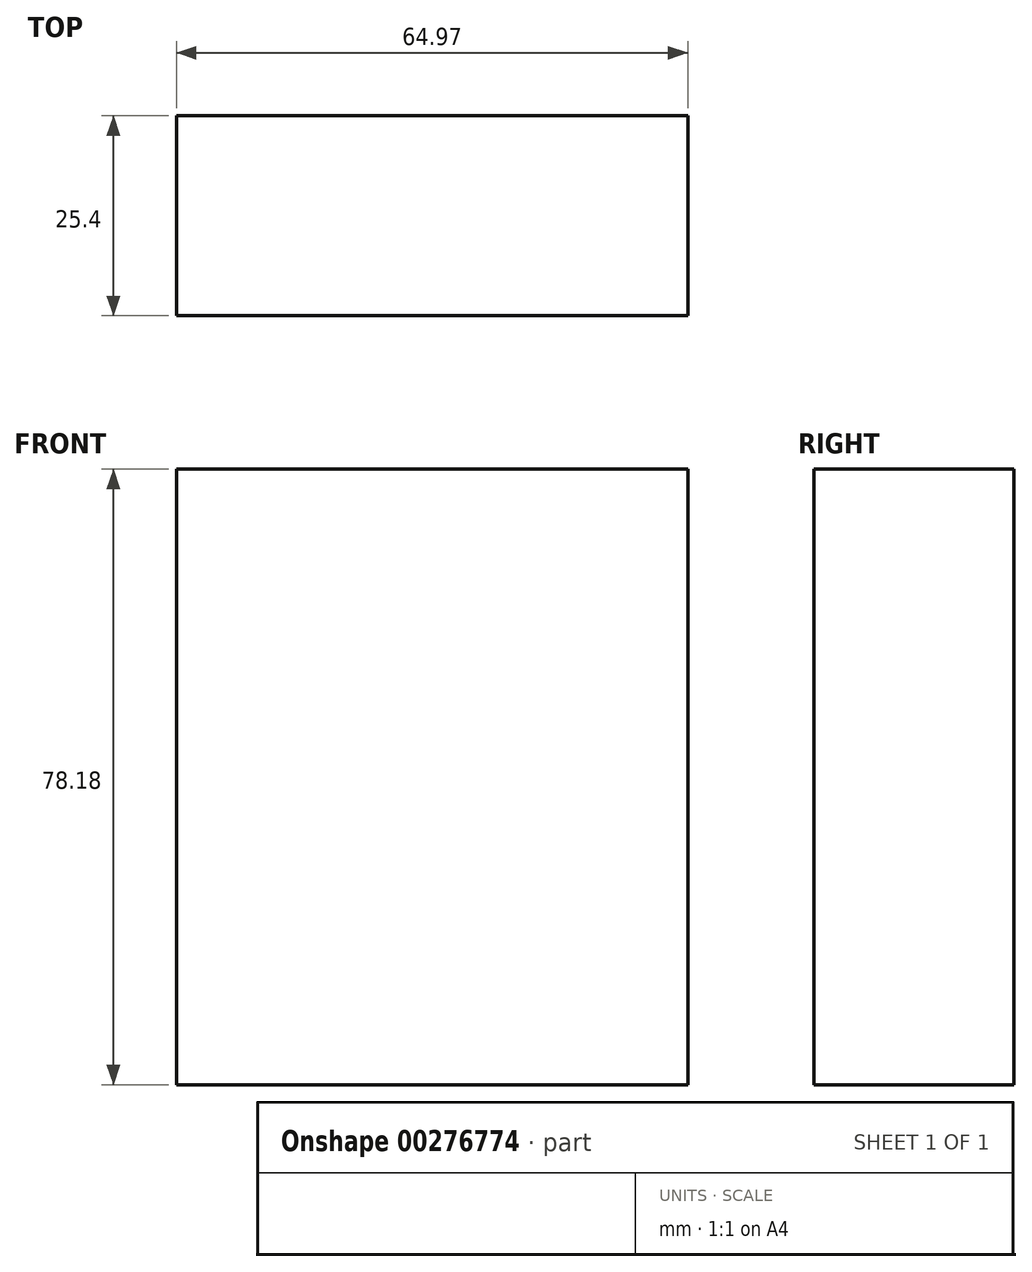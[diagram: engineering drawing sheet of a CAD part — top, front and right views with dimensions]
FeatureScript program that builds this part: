
annotation { "Feature Type Name" : "Feature", "Feature Type Description" : "" }
export const myFeature = defineFeature(function(context is Context, id is Id, definition is map)
    precondition{}
    {
        {
            var Q0;
            Q0=qCreatedBy(makeId("Front.planeOp"),FACE);
            var sketch = newSketch(context, id + "F0", { "sketchPlane" : qUnion([Q0])});
            skLineSegment(sketch, "E0.bottom", {"start": v(-14.77, 56.38) * mm, "end": v(50.2, 56.38) * mm});
            skLineSegment(sketch, "E0.top", {"start": v(-14.77, -21.8) * mm, "end": v(50.2, -21.8) * mm});
            skLineSegment(sketch, "E0.left", {"start": v(-14.77, 56.38) * mm, "end": v(-14.77, -21.8) * mm});
            skLineSegment(sketch, "E0.right", {"start": v(50.2, 56.38) * mm, "end": v(50.2, -21.8) * mm});
            skSolve(sketch);
        }
        {
            var Q0;
            Q0 = qSketchRegion(id + "F0", true);
            extrude(context, id + "F1", {"entities" : qUnion([Q0]), "depth" : 25.4 * mm});
        }
    });
